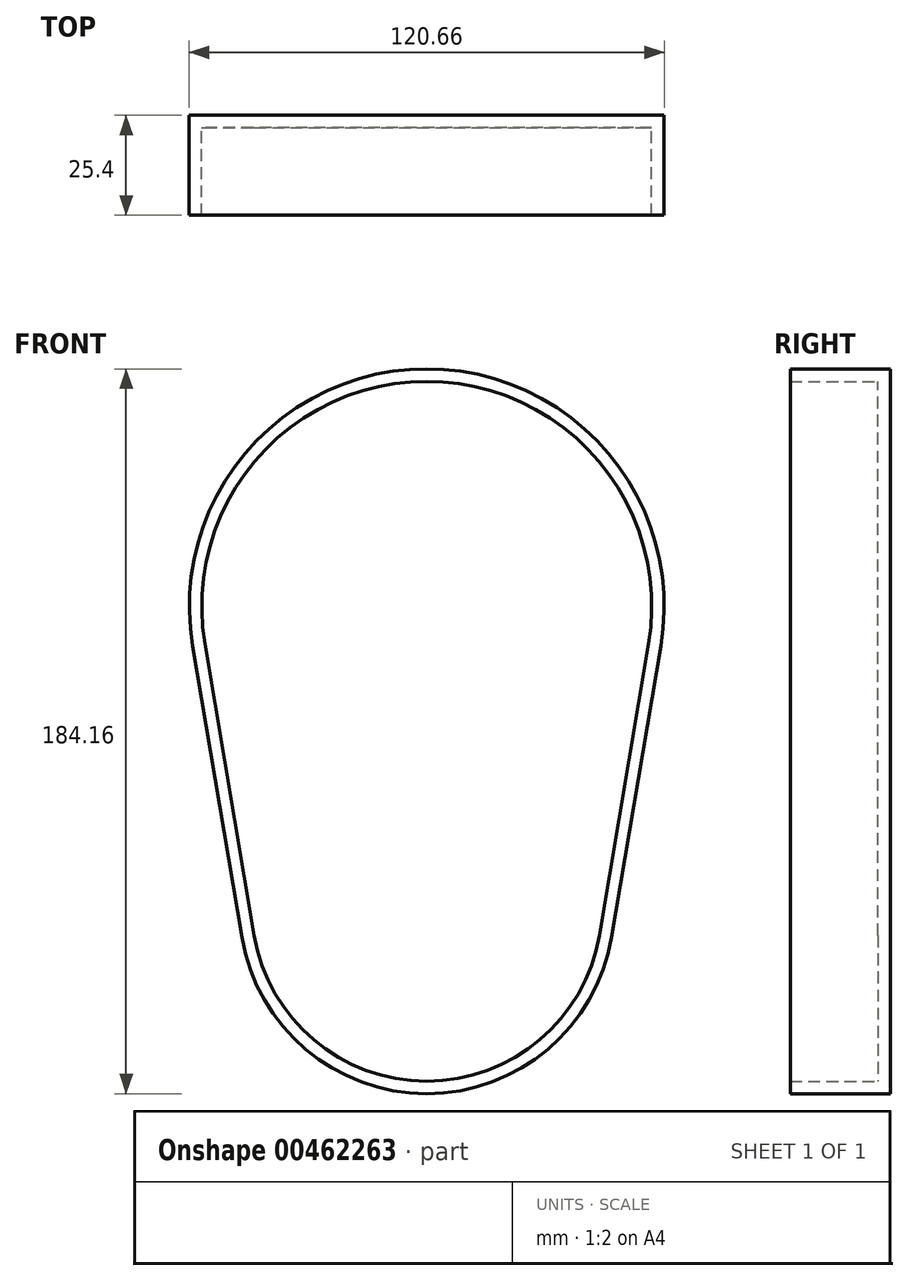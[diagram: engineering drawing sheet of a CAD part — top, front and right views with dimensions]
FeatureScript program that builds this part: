
annotation { "Feature Type Name" : "Feature", "Feature Type Description" : "" }
export const myFeature = defineFeature(function(context is Context, id is Id, definition is map)
    precondition{}
    {
        {
            var Q0;
            Q0=qCreatedBy(makeId("Front.planeOp"),FACE);
            var sketch = newSketch(context, id + "F0", { "sketchPlane" : qUnion([Q0])});
            skLineSegment(sketch, "E0", {"start": v(46.96, -52.39) * mm, "end": v(59.48, 21.7) * mm});
            skArc(sketch, "E1", {"start": v(59.48, 21.7) * mm, "mid": v(0, 92.08) * mm, "end": v(-59.48, 21.7) * mm});
            skLineSegment(sketch, "E2", {"start": v(-59.48, 21.7) * mm, "end": v(-46.96, -52.39) * mm});
            skArc(sketch, "E3", {"start": v(-46.96, -52.39) * mm, "mid": v(0, -92.08) * mm, "end": v(46.96, -52.39) * mm});
            skSolve(sketch);
        }
        {
            var Q0;
            Q0=makeQuery(id+"F0.imprint","IMPRINT",FACE,{"disambiguationData":[TD([[makeQuery(id+"F0.imprint","IMPRINT",EDGE,{"derivedFrom":sQuery(id+"F0.wireOp",EDGE,"E0")}),1.0]])]});
            extrude(context, id + "F1", {"entities" : qUnion([Q0]), "depth" : 25.4 * mm});
        }
        {
            var Q0;
            Q0=makeQuery(id+"F1.opExtrude","CAP_FACE",FACE,{"disambiguationData":[OSD([sQuery(id+"F0.wireOp",EDGE,"E0"),sQuery(id+"F0.wireOp",EDGE,"E1"),sQuery(id+"F0.wireOp",EDGE,"E2"),sQuery(id+"F0.wireOp",EDGE,"E3")])],"isStart":false});
            shell(context, id + "F2", {"entities" : qUnion([Q0]), "thickness" : 3.17 * mm});
        }
    });
